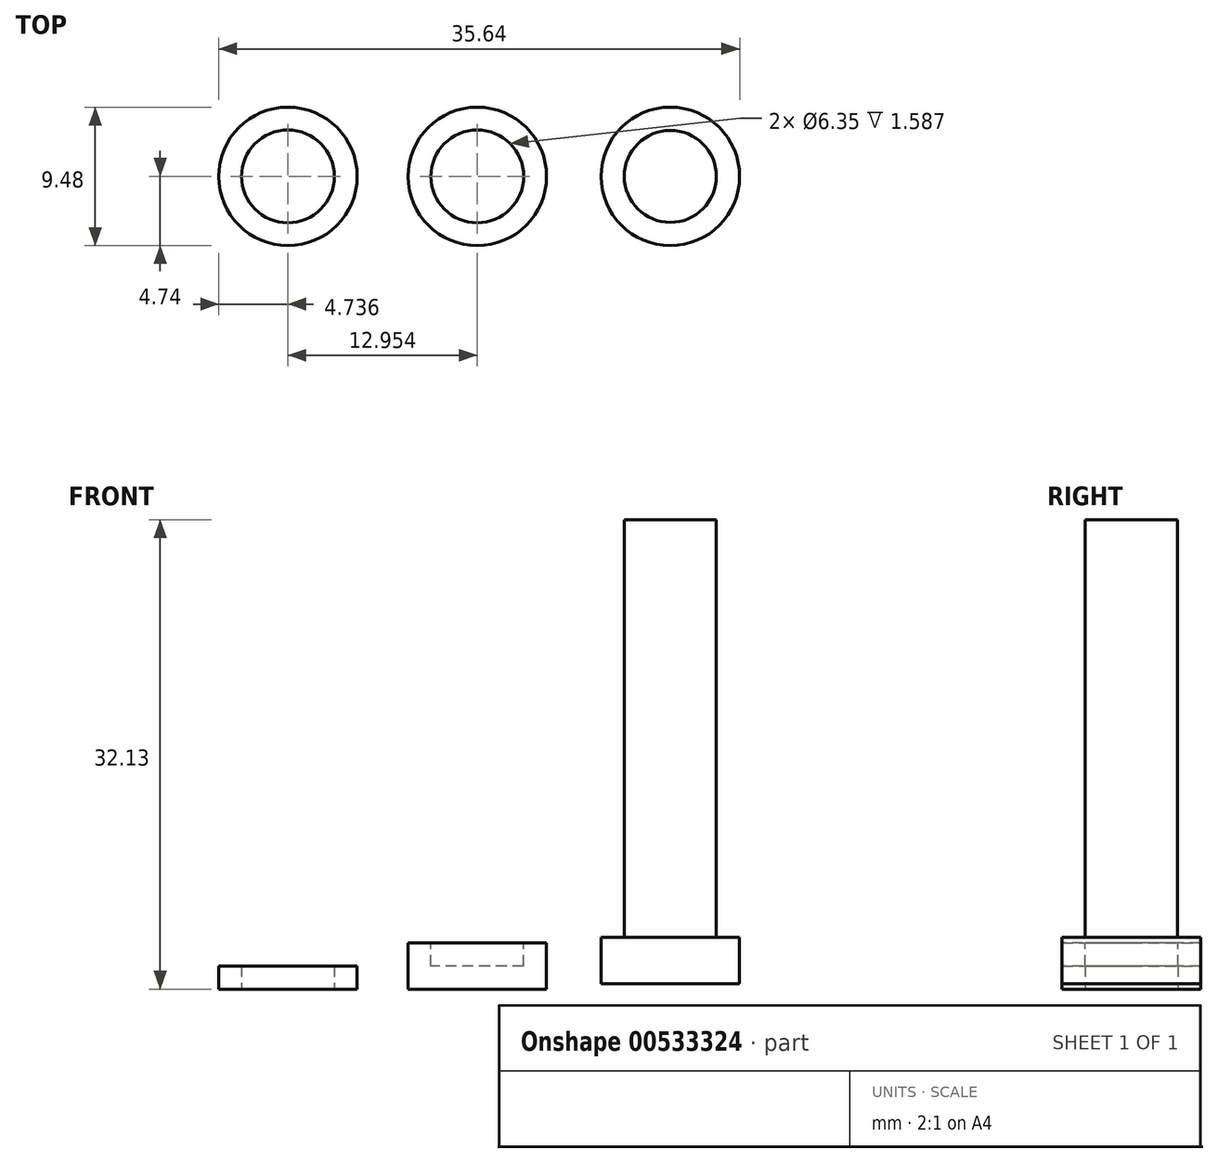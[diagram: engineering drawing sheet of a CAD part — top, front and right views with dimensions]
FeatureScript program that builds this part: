
annotation { "Feature Type Name" : "Feature", "Feature Type Description" : "" }
export const myFeature = defineFeature(function(context is Context, id is Id, definition is map)
    precondition{}
    {
        {
            var Q0;
            Q0=qCreatedBy(makeId("Top.planeOp"),FACE);
            var sketch = newSketch(context, id + "F0", { "sketchPlane" : qUnion([Q0])});
            skCircle(sketch, "E0", {"center": v(0, 0) * mm, "radius": 3.15 * mm});
            skSolve(sketch);
        }
        {
            var Q0;
            Q0=makeQuery(id+"F0.imprint","IMPRINT",FACE,{"disambiguationData":[TD([[makeQuery(id+"F0.imprint","IMPRINT",EDGE,{"derivedFrom":sQuery(id+"F0.wireOp",EDGE,"E0")}),1.0]])]});
            extrude(context, id + "F1", {"entities" : qUnion([Q0]), "depth" : 31.75 * mm, "offsetDistance" : 25.4 * mm});
        }
        {
            var Q0;
            Q0=qCreatedBy(makeId("Top.planeOp"),FACE);
            var sketch = newSketch(context, id + "F2", { "sketchPlane" : qUnion([Q0])});
            skCircle(sketch, "E1", {"center": v(0, 0) * mm, "radius": 4.74 * mm});
            skSolve(sketch);
        }
        {
            var Q0;
            Q0=makeQuery(id+"F2.imprint","IMPRINT",FACE,{"disambiguationData":[TD([[makeQuery(id+"F2.imprint","IMPRINT",EDGE,{"derivedFrom":sQuery(id+"F2.wireOp",EDGE,"E1")}),1.0]])]});
            extrude(context, id + "F3", {"entities" : qUnion([Q0]), "operationType" : NewBodyOperationType.ADD, "oppositeDirection" : true, "depth" : 3.17 * mm, "offsetDistance" : 25.4 * mm});
        }
        {
            var Q0;
            Q0=makeQuery(id+"F1.opExtrude","SWEPT_BODY",BODY,{"disambiguationData":[OSD([sQuery(id+"F0.wireOp",EDGE,"E0")])]});
            transform(context, id + "F4", {"entities" : qUnion([Q0]), "transformType" : TransformType.TRANSLATION_3D, "dx" : 20.83 * mm, "dy" : 0 * mm, "dz" : 0 * mm, "makeCopy" : false});
        }
        {
            var Q0;
            Q0=qCreatedBy(makeId("Top.planeOp"),FACE);
            var sketch = newSketch(context, id + "F5", { "sketchPlane" : qUnion([Q0])});
            skCircle(sketch, "E2", {"center": v(0, 0) * mm, "radius": 4.74 * mm});
            skSolve(sketch);
        }
        {
            var Q0;
            Q0=makeQuery(id+"F5.imprint","IMPRINT",FACE,{"disambiguationData":[TD([[makeQuery(id+"F5.imprint","IMPRINT",EDGE,{"derivedFrom":sQuery(id+"F5.wireOp",EDGE,"E2")}),1.0]])]});
            extrude(context, id + "F6", {"entities" : qUnion([Q0]), "depth" : 3.17 * mm, "offsetDistance" : 25.4 * mm});
        }
        {
            var Q0;
            Q0=qCreatedBy(makeId("Top.planeOp"),FACE);
            var sketch = newSketch(context, id + "F7", { "sketchPlane" : qUnion([Q0])});
            skCircle(sketch, "E3", {"center": v(0, 0) * mm, "radius": 3.18 * mm});
            skSolve(sketch);
        }
        {
            var Q0;
            Q0=makeQuery(id+"F7.imprint","IMPRINT",FACE,{"disambiguationData":[TD([[makeQuery(id+"F7.imprint","IMPRINT",EDGE,{"derivedFrom":sQuery(id+"F7.wireOp",EDGE,"E3")}),1.0]])]});
            extrude(context, id + "F8", {"entities" : qUnion([Q0]), "operationType" : NewBodyOperationType.REMOVE, "depth" : 3.17 * mm, "offsetDistance" : 25.4 * mm});
        }
        {
            var Q0;
            Q0=makeQuery(id+"F6.opExtrude","SWEPT_BODY",BODY,{"disambiguationData":[OSD([sQuery(id+"F5.wireOp",EDGE,"E2")])]});
            transform(context, id + "F9", {"entities" : qUnion([Q0]), "transformType" : TransformType.TRANSLATION_3D, "dx" : 0 * mm, "dy" : 21.34 * mm, "dz" : 0 * mm, "makeCopy" : false});
        }
        {
            var Q0;
            Q0=qCreatedBy(makeId("Top.planeOp"),FACE);
            var sketch = newSketch(context, id + "F10", { "sketchPlane" : qUnion([Q0])});
            skCircle(sketch, "E4", {"center": v(0, 0) * mm, "radius": 4.74 * mm});
            skSolve(sketch);
        }
        {
            var Q0;
            Q0=makeQuery(id+"F10.imprint","IMPRINT",FACE,{"disambiguationData":[TD([[makeQuery(id+"F10.imprint","IMPRINT",EDGE,{"derivedFrom":sQuery(id+"F10.wireOp",EDGE,"E4")}),1.0]])]});
            extrude(context, id + "F11", {"entities" : qUnion([Q0]), "depth" : 3.17 * mm, "offsetDistance" : 25.4 * mm});
        }
        {
            var Q0;
            Q0=qCreatedBy(makeId("Top.planeOp"),FACE);
            var sketch = newSketch(context, id + "F12", { "sketchPlane" : qUnion([Q0])});
            skCircle(sketch, "E5", {"center": v(0, 0) * mm, "radius": 3.18 * mm});
            skSolve(sketch);
        }
        {
            var Q0;
            Q0=makeQuery(id+"F12.imprint","IMPRINT",FACE,{"disambiguationData":[TD([[makeQuery(id+"F12.imprint","IMPRINT",EDGE,{"derivedFrom":sQuery(id+"F12.wireOp",EDGE,"E5")}),1.0]])]});
            extrude(context, id + "F13", {"entities" : qUnion([Q0]), "operationType" : NewBodyOperationType.REMOVE, "depth" : 1.59 * mm, "offsetDistance" : 25.4 * mm});
        }
        {
            var Q0;
            Q0=makeQuery(id+"F6.opExtrude","SWEPT_BODY",BODY,{"disambiguationData":[OSD([sQuery(id+"F5.wireOp",EDGE,"E2")])]});
            transform(context, id + "F14", {"entities" : qUnion([Q0]), "transformType" : TransformType.TRANSLATION_3D, "dx" : -12.95 * mm, "dy" : -21.34 * mm, "dz" : 0 * mm, "makeCopy" : false});
        }
        {
            var Q0;
            Q0=makeQuery(id+"F1.opExtrude","SWEPT_BODY",BODY,{"disambiguationData":[OSD([sQuery(id+"F0.wireOp",EDGE,"E0")])]});
            transform(context, id + "F15", {"entities" : qUnion([Q0]), "transformType" : TransformType.TRANSLATION_3D, "dx" : -7.62 * mm, "dy" : 0 * mm, "dz" : 0 * mm, "makeCopy" : false});
        }
        {
            var Q0;
            Q0=makeQuery(id+"F1.opExtrude","SWEPT_BODY",BODY,{"disambiguationData":[OSD([sQuery(id+"F0.wireOp",EDGE,"E0")])]});
            transform(context, id + "F16", {"entities" : qUnion([Q0]), "transformType" : TransformType.TRANSLATION_3D, "dx" : 0 * mm, "dy" : 0 * mm, "dz" : 3.56 * mm, "makeCopy" : false});
        }
        {
            var Q0;
            Q0=makeQuery(id+"F13.boolean.opBoolean","COPY",FACE,{"derivedFrom":makeQuery(id+"F13.opExtrude","CAP_FACE",FACE,{"disambiguationData":[OSD([sQuery(id+"F12.wireOp",EDGE,"E5")])],"isStart":false})});
            extrude(context, id + "F17", {"entities" : qUnion([Q0]), "operationType" : NewBodyOperationType.ADD, "depth" : 1.59 * mm, "offsetDistance" : 25.4 * mm});
        }
        {
            var Q0;
            Q0=makeQuery(id+"F6.opExtrude","CAP_FACE",FACE,{"disambiguationData":[OSD([sQuery(id+"F5.wireOp",EDGE,"E2")])],"isStart":false});
            extrude(context, id + "F18", {"entities" : qUnion([Q0]), "operationType" : NewBodyOperationType.REMOVE, "oppositeDirection" : true, "depth" : 1.59 * mm, "offsetDistance" : 25.4 * mm});
        }
        {
            var Q0;
            Q0=makeQuery(id+"F11.opExtrude","CAP_FACE",FACE,{"disambiguationData":[OSD([sQuery(id+"F10.wireOp",EDGE,"E4")])],"isStart":false});
            var sketch = newSketch(context, id + "F19", { "sketchPlane" : qUnion([Q0])});
            skCircle(sketch, "E6", {"center": v(0, 0) * mm, "radius": 3.18 * mm});
            skSolve(sketch);
        }
        {
            var Q0;
            Q0=makeQuery(id+"F19.imprint","IMPRINT",FACE,{"disambiguationData":[TD([[makeQuery(id+"F19.imprint","IMPRINT",EDGE,{"derivedFrom":sQuery(id+"F19.wireOp",EDGE,"E6")}),1.0]])]});
            extrude(context, id + "F20", {"entities" : qUnion([Q0]), "operationType" : NewBodyOperationType.REMOVE, "oppositeDirection" : true, "depth" : 1.59 * mm, "offsetDistance" : 25.4 * mm});
        }
        {
            var Q0;
            Q0=makeQuery(id+"F1.opExtrude","CAP_FACE",FACE,{"disambiguationData":[OSD([sQuery(id+"F0.wireOp",EDGE,"E0")])],"isStart":false});
            extrude(context, id + "F21", {"entities" : qUnion([Q0]), "operationType" : NewBodyOperationType.REMOVE, "oppositeDirection" : true, "depth" : 3.17 * mm, "offsetDistance" : 25.4 * mm});
        }
    });
